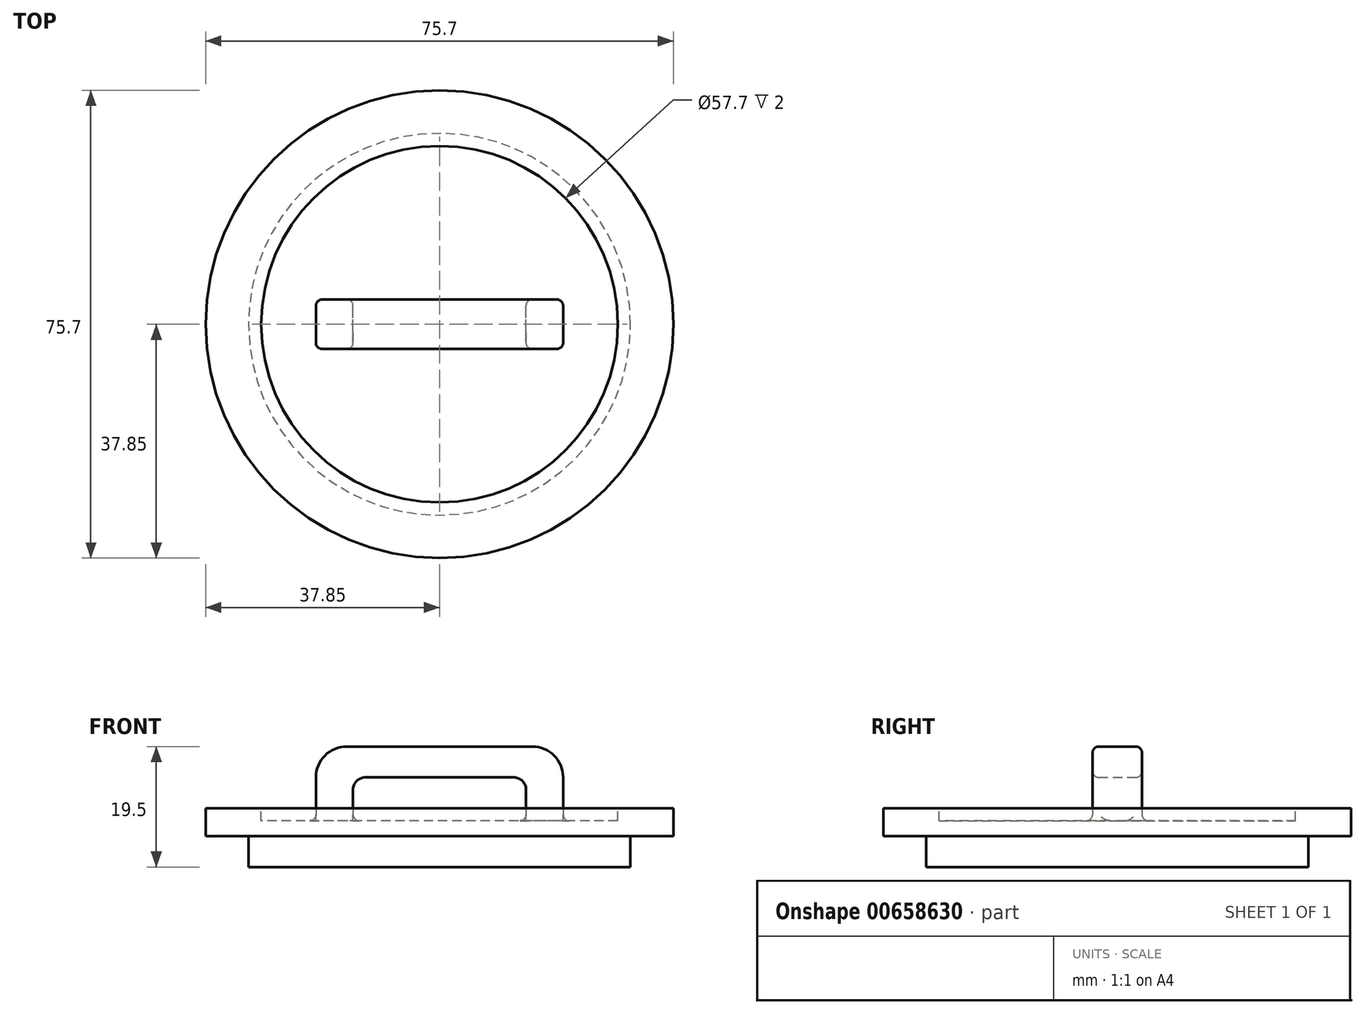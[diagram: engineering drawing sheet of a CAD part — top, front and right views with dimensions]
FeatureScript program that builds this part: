
annotation { "Feature Type Name" : "Feature", "Feature Type Description" : "" }
export const myFeature = defineFeature(function(context is Context, id is Id, definition is map)
    precondition{}
    {
        {
            var Q0;
            Q0=qCreatedBy(makeId("Top.planeOp"),FACE);
            cPlane(context, id + "F0", {"entities" : qUnion([Q0]), "cplaneType" : CPlaneType.OFFSET, "offset" : 0 * mm, "width" : 150 * mm, "height" : 150 * mm});
        }
        {
            var Q0;
            Q0=qCreatedBy(id+"F0.planeOp",FACE);
            var sketch = newSketch(context, id + "F1", { "sketchPlane" : qUnion([Q0])});
            skCircle(sketch, "E0", {"center": v(0, 0) * mm, "radius": 30.9 * mm});
            skSolve(sketch);
        }
        {
            var Q0;
            Q0 = qSketchRegion(id + "F1", true);
            extrude(context, id + "F2", {"entities" : qUnion([Q0]), "depth" : 5 * mm, "offsetDistance" : 25 * mm});
        }
        {
            var Q0;
            Q0=makeQuery(id+"F2.opExtrude","CAP_FACE",FACE,{"disambiguationData":[OSD([sQuery(id+"F1.wireOp",EDGE,"E0")])],"isStart":false});
            var sketch = newSketch(context, id + "F3", { "sketchPlane" : qUnion([Q0])});
            skCircle(sketch, "E1", {"center": v(0, 0) * mm, "radius": 37.85 * mm});
            skSolve(sketch);
        }
        {
            var Q0;
            Q0 = qSketchRegion(id + "F3", true);
            extrude(context, id + "F4", {"entities" : qUnion([Q0]), "operationType" : NewBodyOperationType.ADD, "depth" : 4.5 * mm, "offsetDistance" : 25 * mm});
        }
        {
            var Q0;
            Q0=makeQuery(id+"F4.opExtrude","CAP_FACE",FACE,{"disambiguationData":[OSD([sQuery(id+"F3.wireOp",EDGE,"E1")])],"isStart":false});
            var sketch = newSketch(context, id + "F5", { "sketchPlane" : qUnion([Q0])});
            skCircle(sketch, "E2", {"center": v(0, 0) * mm, "radius": 28.85 * mm});
            skSolve(sketch);
        }
        {
            var Q0;
            Q0=makeQuery(id+"F5.imprint","IMPRINT",FACE,{"disambiguationData":[TD([[makeQuery(id+"F5.imprint","IMPRINT",EDGE,{"derivedFrom":sQuery(id+"F5.wireOp",EDGE,"E2")}),1.0]])]});
            extrude(context, id + "F6", {"entities" : qUnion([Q0]), "operationType" : NewBodyOperationType.REMOVE, "oppositeDirection" : true, "depth" : 2 * mm, "offsetDistance" : 25 * mm});
        }
        {
            var Q0;
            Q0=makeQuery(id+"F6.boolean.opBoolean","COPY",FACE,{"derivedFrom":makeQuery(id+"F6.opExtrude","CAP_FACE",FACE,{"disambiguationData":[OSD([sQuery(id+"F5.wireOp",EDGE,"E2")])],"isStart":false})});
            var sketch = newSketch(context, id + "F7", { "sketchPlane" : qUnion([Q0])});
            skLineSegment(sketch, "E3.bottom", {"start": v(20, 4) * mm, "end": v(-20, 4) * mm});
            skLineSegment(sketch, "E3.top", {"start": v(20, -4) * mm, "end": v(-20, -4) * mm});
            skLineSegment(sketch, "E3.left", {"start": v(20, 4) * mm, "end": v(20, -4) * mm});
            skLineSegment(sketch, "E3.right", {"start": v(-20, 4) * mm, "end": v(-20, -4) * mm});
            skPoint(sketch, "E3.middle", {"position": v(0, 0) * mm});
            skSolve(sketch);
        }
        {
            var Q0;
            Q0=makeQuery(id+"F7.imprint","IMPRINT",FACE,{"disambiguationData":[TD([[makeQuery(id+"F7.imprint","IMPRINT",EDGE,{"derivedFrom":sQuery(id+"F7.wireOp",EDGE,"E3.bottom")}),1.0]])]});
            var sketch = newSketch(context, id + "F8", { "sketchPlane" : qUnion([Q0])});
            skLineSegment(sketch, "E4.bottom", {"start": v(14, -4) * mm, "end": v(-14, -4) * mm});
            skLineSegment(sketch, "E4.top", {"start": v(14, 4) * mm, "end": v(-14, 4) * mm});
            skLineSegment(sketch, "E4.left", {"start": v(14, -4) * mm, "end": v(14, 4) * mm});
            skLineSegment(sketch, "E4.right", {"start": v(-14, -4) * mm, "end": v(-14, 4) * mm});
            skPoint(sketch, "E4.middle", {"position": v(0, 0) * mm});
            skSolve(sketch);
        }
        {
            var Q0;
            Q0=makeQuery(id+"F7.imprint","IMPRINT",FACE,{"disambiguationData":[TD([[makeQuery(id+"F7.imprint","IMPRINT",EDGE,{"derivedFrom":sQuery(id+"F7.wireOp",EDGE,"E3.bottom")}),1.0]])]});
            extrude(context, id + "F9", {"entities" : qUnion([Q0]), "operationType" : NewBodyOperationType.ADD, "depth" : 12 * mm, "offsetDistance" : 25 * mm});
        }
        {
            var Q0;
            Q0=makeQuery(id+"F9.opExtrude","CAP_EDGE",EDGE,{"disambiguationData":[OSD([sQuery(id+"F7.wireOp",EDGE,"E3.right")])],"isStart":false});
            var Q1;
            Q1=makeQuery(id+"F9.opExtrude","CAP_EDGE",EDGE,{"disambiguationData":[OSD([sQuery(id+"F7.wireOp",EDGE,"E3.left")])],"isStart":false});
            fillet(context, id + "F10", {"entities" : qUnion([Q0, Q1]), "radius" : 5 * mm, "tangentPropagation" : true, "allowEdgeOverflow" : false});
        }
        {
            var Q0;
            Q0 = qSketchRegion(id + "F8", true);
            extrude(context, id + "F11", {"entities" : qUnion([Q0]), "operationType" : NewBodyOperationType.REMOVE, "depth" : 7 * mm, "offsetDistance" : 25 * mm});
        }
        {
            var Q0;
            Q0=makeQuery(id+"F11.boolean.opBoolean","COPY",EDGE,{"derivedFrom":makeQuery(id+"F11.opExtrude","CAP_EDGE",EDGE,{"disambiguationData":[OSD([sQuery(id+"F8.wireOp",EDGE,"E4.right")])],"isStart":false})});
            var Q1;
            Q1=makeQuery(id+"F11.boolean.opBoolean","COPY",EDGE,{"derivedFrom":makeQuery(id+"F11.opExtrude","CAP_EDGE",EDGE,{"disambiguationData":[OSD([sQuery(id+"F8.wireOp",EDGE,"E4.left")])],"isStart":false})});
            fillet(context, id + "F12", {"entities" : qUnion([Q0, Q1]), "radius" : 2 * mm, "tangentPropagation" : true, "allowEdgeOverflow" : false});
        }
        {
            var Q0;
            Q0=makeQuery(id+"F9.opExtrude","CAP_EDGE",EDGE,{"disambiguationData":[OSD([sQuery(id+"F7.wireOp",EDGE,"E3.top")])],"isStart":false});
            var Q1;
            Q1=makeQuery(id+"F11.boolean.opBoolean","COPY",EDGE,{"derivedFrom":makeQuery(id+"F11.opExtrude","SWEPT_EDGE",EDGE,{"disambiguationData":[OSD([sQuery(id+"F7.wireOp",EDGE,"E3.top"),sQuery(id+"F8.wireOp",EDGE,"E4.bottom"),sQuery(id+"F8.wireOp",EDGE,"E4.left")])]})});
            var Q2;
            Q2=makeQuery(id+"F12.opFillet","BLEND_EDGE",EDGE,{"blendedFrom":[makeQuery(id+"F11.boolean.opBoolean","COPY",EDGE,{"derivedFrom":makeQuery(id+"F11.opExtrude","CAP_EDGE",EDGE,{"disambiguationData":[OSD([sQuery(id+"F8.wireOp",EDGE,"E4.left")])],"isStart":false})}),makeQuery(id+"F9.opExtrude","SWEPT_FACE",FACE,{"disambiguationData":[OSD([sQuery(id+"F7.wireOp",EDGE,"E3.top")])]})],"blendedInto":[makeQuery(id+"F9.opExtrude","SWEPT_FACE",FACE,{"disambiguationData":[OSD([sQuery(id+"F7.wireOp",EDGE,"E3.top")])]})]});
            var Q3;
            Q3=makeQuery(id+"F11.boolean.opBoolean","COPY",EDGE,{"derivedFrom":makeQuery(id+"F11.opExtrude","CAP_EDGE",EDGE,{"disambiguationData":[OSD([sQuery(id+"F8.wireOp",EDGE,"E4.bottom")])],"isStart":false})});
            var Q4;
            Q4=makeQuery(id+"F12.opFillet","BLEND_EDGE",EDGE,{"blendedFrom":[makeQuery(id+"F11.boolean.opBoolean","COPY",EDGE,{"derivedFrom":makeQuery(id+"F11.opExtrude","CAP_EDGE",EDGE,{"disambiguationData":[OSD([sQuery(id+"F8.wireOp",EDGE,"E4.right")])],"isStart":false})}),makeQuery(id+"F9.opExtrude","SWEPT_FACE",FACE,{"disambiguationData":[OSD([sQuery(id+"F7.wireOp",EDGE,"E3.top")])]})],"blendedInto":[makeQuery(id+"F9.opExtrude","SWEPT_FACE",FACE,{"disambiguationData":[OSD([sQuery(id+"F7.wireOp",EDGE,"E3.top")])]})]});
            var Q5;
            Q5=makeQuery(id+"F9.opExtrude","SWEPT_FACE",FACE,{"disambiguationData":[OSD([sQuery(id+"F7.wireOp",EDGE,"E3.top")])]});
            var Q6;
            Q6=makeQuery(id+"F9.opExtrude","SWEPT_FACE",FACE,{"disambiguationData":[OSD([sQuery(id+"F7.wireOp",EDGE,"E3.bottom")])]});
            fillet(context, id + "F13", {"entities" : qUnion([Q0, Q1, Q2, Q3, Q4, Q5, Q6]), "radius" : 1 * mm, "tangentPropagation" : true, "allowEdgeOverflow" : false});
        }
    });
